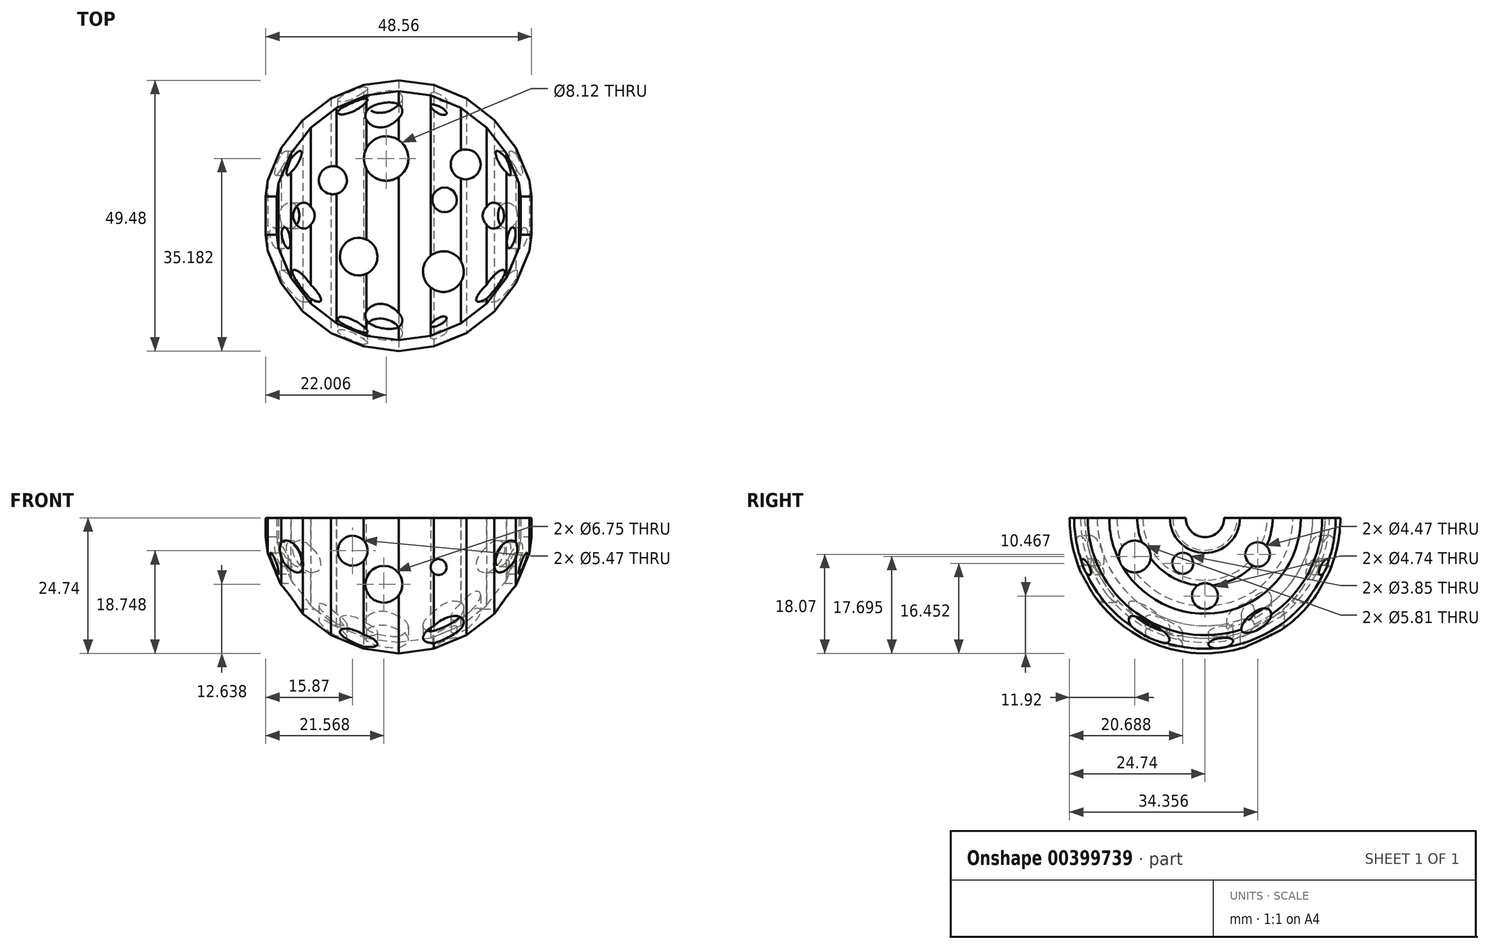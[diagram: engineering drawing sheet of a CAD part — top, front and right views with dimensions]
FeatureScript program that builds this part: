
annotation { "Feature Type Name" : "Feature", "Feature Type Description" : "" }
export const myFeature = defineFeature(function(context is Context, id is Id, definition is map)
    precondition{}
    {
        {
            var Q0;
            Q0=qCreatedBy(makeId("Top.planeOp"),FACE);
            var sketch = newSketch(context, id + "F0", { "sketchPlane" : qUnion([Q0])});
            skLineSegment(sketch, "E0", {"start": v(-24.74, 0) * mm, "end": v(24.74, 0) * mm});
            skLineSegment(sketch, "E1", {"start": v(-24.74, 0) * mm, "end": v(-22.74, 0) * mm});
            skLineSegment(sketch, "E2", {"start": v(24.74, 0) * mm, "end": v(22.74, 0) * mm});
            skLineSegment(sketch, "E3", {"start": v(0, 0) * mm, "end": v(-21.43, -12.37) * mm});
            skLineSegment(sketch, "E4", {"start": v(0, 0) * mm, "end": v(-23.9, -6.4) * mm});
            skLineSegment(sketch, "E5", {"start": v(-23.9, -6.4) * mm, "end": v(0, 0) * mm});
            skLineSegment(sketch, "E6", {"start": v(0, 0) * mm, "end": v(-17.5, -17.5) * mm});
            skLineSegment(sketch, "E7", {"start": v(-17.5, -17.5) * mm, "end": v(0, 0) * mm});
            skLineSegment(sketch, "E8", {"start": v(0, 0) * mm, "end": v(12.37, -21.43) * mm});
            skLineSegment(sketch, "E9", {"start": v(12.37, -21.43) * mm, "end": v(0, 0) * mm});
            skLineSegment(sketch, "E10", {"start": v(0, 0) * mm, "end": v(17.5, -17.5) * mm});
            skLineSegment(sketch, "E11", {"start": v(17.5, -17.5) * mm, "end": v(0, 0) * mm});
            skLineSegment(sketch, "E12", {"start": v(0, 0) * mm, "end": v(21.43, -12.37) * mm});
            skLineSegment(sketch, "E13", {"start": v(0, 0) * mm, "end": v(-12.37, -21.43) * mm});
            skLineSegment(sketch, "E14", {"start": v(-12.37, -21.43) * mm, "end": v(0, 0) * mm});
            skLineSegment(sketch, "E15", {"start": v(0, 0) * mm, "end": v(-6.4, -23.9) * mm});
            skLineSegment(sketch, "E16", {"start": v(0, 0) * mm, "end": v(6.4, -23.9) * mm});
            skLineSegment(sketch, "E17", {"start": v(0, 0) * mm, "end": v(23.9, -6.4) * mm});
            skLineSegment(sketch, "E18", {"start": v(0, 0) * mm, "end": v(0, -24.74) * mm});
            skSolve(sketch);
        }
        {
            var Q0;
            Q0=qCreatedBy(makeId("Top.planeOp"),FACE);
            var sketch = newSketch(context, id + "F1", { "sketchPlane" : qUnion([Q0])});
            skLineSegment(sketch, "E19", {"start": v(-24.74, 0) * mm, "end": v(-23.9, -6.4) * mm});
            skLineSegment(sketch, "E20", {"start": v(-23.9, -6.4) * mm, "end": v(-21.43, -12.37) * mm});
            skLineSegment(sketch, "E21", {"start": v(-21.43, -12.37) * mm, "end": v(-17.5, -17.5) * mm});
            skLineSegment(sketch, "E22", {"start": v(-17.5, -17.5) * mm, "end": v(-12.37, -21.43) * mm});
            skLineSegment(sketch, "E23", {"start": v(-12.37, -21.43) * mm, "end": v(-6.4, -23.9) * mm});
            skLineSegment(sketch, "E24", {"start": v(-6.4, -23.9) * mm, "end": v(0, -24.74) * mm});
            skLineSegment(sketch, "E25", {"start": v(0, -24.74) * mm, "end": v(6.4, -23.9) * mm});
            skLineSegment(sketch, "E26", {"start": v(6.4, -23.9) * mm, "end": v(12.37, -21.43) * mm});
            skLineSegment(sketch, "E27", {"start": v(12.37, -21.43) * mm, "end": v(17.5, -17.5) * mm});
            skLineSegment(sketch, "E28", {"start": v(17.5, -17.5) * mm, "end": v(21.43, -12.37) * mm});
            skLineSegment(sketch, "E29", {"start": v(21.43, -12.37) * mm, "end": v(23.9, -6.4) * mm});
            skLineSegment(sketch, "E30", {"start": v(23.9, -6.4) * mm, "end": v(24.74, 0) * mm});
            skLineSegment(sketch, "E31", {"start": v(-22.74, 0) * mm, "end": v(-21.97, -5.89) * mm});
            skLineSegment(sketch, "E32", {"start": v(-21.97, -5.89) * mm, "end": v(-19.7, -11.37) * mm});
            skLineSegment(sketch, "E33", {"start": v(-19.7, -11.37) * mm, "end": v(-16.08, -16.08) * mm});
            skLineSegment(sketch, "E34", {"start": v(-16.08, -16.08) * mm, "end": v(-11.37, -19.7) * mm});
            skLineSegment(sketch, "E35", {"start": v(-11.37, -19.7) * mm, "end": v(-5.89, -21.97) * mm});
            skLineSegment(sketch, "E36", {"start": v(-5.89, -21.97) * mm, "end": v(0, -22.74) * mm});
            skLineSegment(sketch, "E37", {"start": v(0, -22.74) * mm, "end": v(5.89, -21.97) * mm});
            skLineSegment(sketch, "E38", {"start": v(5.89, -21.97) * mm, "end": v(11.37, -19.7) * mm});
            skLineSegment(sketch, "E39", {"start": v(11.37, -19.7) * mm, "end": v(16.08, -16.08) * mm});
            skLineSegment(sketch, "E40", {"start": v(16.08, -16.08) * mm, "end": v(19.7, -11.37) * mm});
            skLineSegment(sketch, "E41", {"start": v(19.7, -11.37) * mm, "end": v(21.97, -5.89) * mm});
            skLineSegment(sketch, "E42", {"start": v(21.97, -5.89) * mm, "end": v(22.74, 0) * mm});
            skLineSegment(sketch, "E43", {"start": v(-24.74, 0) * mm, "end": v(-22.74, 0) * mm});
            skLineSegment(sketch, "E44", {"start": v(22.74, 0) * mm, "end": v(24.74, 0) * mm});
            skSolve(sketch);
        }
        {
            var Q0;
            Q0=qSketchRegion(id+"F1",true);
            var Q1;
            Q1=sQuery(id+"F0.wireOp",EDGE,"E0");
            revolve(context, id + "F2", {"entities" : qUnion([Q0]), "axis" : qUnion([Q1]), "revolveType" : RevolveType.FULL});
        }
        {
            var Q0;
            Q0=qCreatedBy(makeId("Top.planeOp"),FACE);
            var sketch = newSketch(context, id + "F3", { "sketchPlane" : qUnion([Q0])});
            skLineSegment(sketch, "E45.bottom", {"start": v(-24.99, 25) * mm, "end": v(24.99, 25) * mm});
            skLineSegment(sketch, "E45.top", {"start": v(-24.99, -25) * mm, "end": v(24.99, -25) * mm});
            skLineSegment(sketch, "E45.left", {"start": v(-24.99, 25) * mm, "end": v(-24.99, -25) * mm});
            skLineSegment(sketch, "E45.right", {"start": v(24.99, 25) * mm, "end": v(24.99, -25) * mm});
            skPoint(sketch, "E45.middle", {"position": v(0, 0) * mm});
            skSolve(sketch);
        }
        {
            var Q0;
            Q0=qSketchRegion(id+"F3",true);
            extrude(context, id + "F4", {"entities" : qUnion([Q0]), "operationType" : NewBodyOperationType.REMOVE, "depth" : 25 * mm});
        }
        {
            var Q0;
            Q0=qCreatedBy(makeId("Top.planeOp"),FACE);
            var sketch = newSketch(context, id + "F5", { "sketchPlane" : qUnion([Q0])});
            skLineSegment(sketch, "E46.bottom", {"start": v(-27.5, 27.5) * mm, "end": v(27.5, 27.5) * mm});
            skLineSegment(sketch, "E46.top", {"start": v(-27.5, -27.5) * mm, "end": v(27.5, -27.5) * mm});
            skLineSegment(sketch, "E46.left", {"start": v(-27.5, 27.5) * mm, "end": v(-27.5, -27.5) * mm});
            skLineSegment(sketch, "E46.right", {"start": v(27.5, 27.5) * mm, "end": v(27.5, -27.5) * mm});
            skPoint(sketch, "E46.middle", {"position": v(0, 0) * mm});
            skSolve(sketch);
        }
        {
            var Q0;
            Q0=qCreatedBy(makeId("Top.planeOp"),FACE);
            var sketch = newSketch(context, id + "F6", { "sketchPlane" : qUnion([Q0])});
            skLineSegment(sketch, "E47.bottom", {"start": v(-30, 30) * mm, "end": v(30, 30) * mm});
            skLineSegment(sketch, "E47.top", {"start": v(-30, -30) * mm, "end": v(30, -30) * mm});
            skLineSegment(sketch, "E47.left", {"start": v(-30, 30) * mm, "end": v(-30, -30) * mm});
            skLineSegment(sketch, "E47.right", {"start": v(30, 30) * mm, "end": v(30, -30) * mm});
            skPoint(sketch, "E47.middle", {"position": v(0, 0) * mm});
            skSolve(sketch);
        }
        {
            var Q0;
            Q0=qCreatedBy(makeId("Right.planeOp"),FACE);
            var sketch = newSketch(context, id + "F7", { "sketchPlane" : qUnion([Q0])});
            skCircle(sketch, "E48", {"center": v(0, 0) * mm, "radius": 3.5 * mm});
            skSolve(sketch);
        }
        {
            var Q0;
            Q0=qSketchRegion(id+"F7",true);
            extrude(context, id + "F8", {"entities" : qUnion([Q0]), "operationType" : NewBodyOperationType.REMOVE, "depth" : 25 * mm, "hasSecondDirection" : true, "secondDirectionOppositeDirection" : true, "secondDirectionDepth" : 25 * mm});
        }
        {
            var Q0;
            Q0=qCreatedBy(makeId("Top.planeOp"),FACE);
            var sketch = newSketch(context, id + "F9", { "sketchPlane" : qUnion([Q0])});
            skCircle(sketch, "E49", {"center": v(8.17, -10.22) * mm, "radius": 3.72 * mm});
            skCircle(sketch, "E50", {"center": v(-7.31, -7.48) * mm, "radius": 3.44 * mm});
            skCircle(sketch, "E51", {"center": v(-12.03, 6.48) * mm, "radius": 2.57 * mm});
            skCircle(sketch, "E52", {"center": v(-2.27, 10.44) * mm, "radius": 4.06 * mm});
            skCircle(sketch, "E53", {"center": v(8.4, 2.88) * mm, "radius": 2.25 * mm});
            skCircle(sketch, "E54", {"center": v(12.25, 9.37) * mm, "radius": 2.73 * mm});
            skSolve(sketch);
        }
        {
            var Q0;
            Q0=qSketchRegion(id+"F9",true);
            extrude(context, id + "F10", {"entities" : qUnion([Q0]), "operationType" : NewBodyOperationType.REMOVE, "depth" : 25 * mm, "hasSecondDirection" : true, "secondDirectionOppositeDirection" : true, "secondDirectionDepth" : 25 * mm});
        }
        {
            var Q0;
            Q0=qCreatedBy(makeId("Right.planeOp"),FACE);
            var sketch = newSketch(context, id + "F11", { "sketchPlane" : qUnion([Q0])});
            skCircle(sketch, "E55", {"center": v(-12.82, -7.05) * mm, "radius": 2.9 * mm});
            skCircle(sketch, "E56", {"center": v(-4.05, -8.29) * mm, "radius": 1.93 * mm});
            skCircle(sketch, "E57", {"center": v(0, -14.27) * mm, "radius": 2.37 * mm});
            skCircle(sketch, "E58", {"center": v(9.62, -6.67) * mm, "radius": 2.24 * mm});
            skCircle(sketch, "E59", {"center": v(4.9, 10.82) * mm, "radius": 2.26 * mm});
            skCircle(sketch, "E60", {"center": v(17.17, 4.25) * mm, "radius": 2.33 * mm});
            skCircle(sketch, "E61", {"center": v(-9.87, 7.03) * mm, "radius": 2.43 * mm});
            skSolve(sketch);
        }
        {
            var Q0;
            Q0=qSketchRegion(id+"F11",true);
            extrude(context, id + "F12", {"entities" : qUnion([Q0]), "operationType" : NewBodyOperationType.REMOVE, "oppositeDirection" : true, "depth" : 25 * mm, "hasSecondDirection" : true, "secondDirectionOppositeDirection" : false, "secondDirectionDepth" : 25 * mm});
        }
        {
            var Q0;
            Q0=qCreatedBy(makeId("Front.planeOp"),FACE);
            var sketch = newSketch(context, id + "F13", { "sketchPlane" : qUnion([Q0])});
            skCircle(sketch, "E62", {"center": v(-8.4, -6) * mm, "radius": 2.73 * mm});
            skCircle(sketch, "E63", {"center": v(-2.71, -12.1) * mm, "radius": 3.38 * mm});
            skCircle(sketch, "E64", {"center": v(7.3, -8.97) * mm, "radius": 1.45 * mm});
            skCircle(sketch, "E65", {"center": v(8.58, 6.17) * mm, "radius": 3.57 * mm});
            skCircle(sketch, "E66", {"center": v(-2.54, 6.65) * mm, "radius": 2.53 * mm});
            skCircle(sketch, "E67", {"center": v(-10.55, 10.22) * mm, "radius": 2.94 * mm});
            skSolve(sketch);
        }
        {
            var Q0;
            Q0=qSketchRegion(id+"F13",true);
            extrude(context, id + "F14", {"entities" : qUnion([Q0]), "operationType" : NewBodyOperationType.REMOVE, "oppositeDirection" : true, "depth" : 25 * mm, "hasSecondDirection" : true, "secondDirectionOppositeDirection" : false, "secondDirectionDepth" : 25 * mm});
        }
    });
